# Revit family: C-Channel
name_source: partatom
category: Structural Framing
revit_build: Autodesk Revit Architecture 2012 (Build: 20110210_1515)
units: mm (PartAtom-declared; Revit-internal decimal feet)

## types (32) — shared parameters
Assembly Code = B10

## per-type parameters (varying)
| type | A | W | bf | d | tf | tw | x |
| C15X50 | 14.7 in² | 50 | 0' - 3 3/4" | 1' - 3" | 0' - 0 5/8" | 0' - 0 11/16" | 0' - 0 13/16" |
| C15X40 | 11.8 in² | 40 | 0' - 3 1/2" | 1' - 3" | 0' - 0 5/8" | 0' - 0 1/2" | 0' - 0 3/4" |
| C15X33.9 | 10 in² | 33.9 | 0' - 3 3/8" | 1' - 3" | 0' - 0 5/8" | 0' - 0 3/8" | 0' - 0 13/16" |
| C12X30 | 8.81 in² | 30 | 0' - 3 3/16" | 1' - 0" | 0' - 0 1/2" | 0' - 0 1/2" | 0' - 0 11/16" |
| C12X25 | 7.34 in² | 25 | 0' - 3 1/16" | 1' - 0" | 0' - 0 1/2" | 0' - 0 3/8" | 0' - 0 11/16" |
| C12X20.7 | 6.08 in² | 20.7 | 0' - 2 15/16" | 1' - 0" | 0' - 0 1/2" | 0' - 0 5/16" | 0' - 0 11/16" |
| C10X30 | 8.81 in² | 30 | 0' - 3" | 0' - 10" | 0' - 0 7/16" | 0' - 0 11/16" | 0' - 0 5/8" |
| C10X25 | 7.34 in² | 25 | 0' - 2 7/8" | 0' - 10" | 0' - 0 7/16" | 0' - 0 1/2" | 0' - 0 5/8" |
| C10X20 | 5.87 in² | 20 | 0' - 2 3/4" | 0' - 10" | 0' - 0 7/16" | 0' - 0 3/8" | 0' - 0 5/8" |
| C10X15.3 | 4.48 in² | 15.3 | 0' - 2 5/8" | 0' - 10" | 0' - 0 7/16" | 0' - 0 1/4" | 0' - 0 5/8" |
| C9X20 | 5.87 in² | 20 | 0' - 2 5/8" | 0' - 9" | 0' - 0 7/16" | 0' - 0 7/16" | 0' - 0 9/16" |
| C9X15 | 4.41 in² | 15 | 0' - 2 1/2" | 0' - 9" | 0' - 0 7/16" | 0' - 0 5/16" | 0' - 0 9/16" |
| C9X13.4 | 3.94 in² | 13.4 | 0' - 2 7/16" | 0' - 9" | 0' - 0 7/16" | 0' - 0 1/4" | 0' - 0 5/8" |
| C8X18.7 | 5.51 in² | 18.7 | 0' - 2 1/2" | 0' - 8" | 0' - 0 3/8" | 0' - 0 1/2" | 0' - 0 9/16" |
| C8X18.5 - Obsolete | 5.5 in² | 18.75 | 0' - 2 1/2" | 0' - 8" | 0' - 0 3/8" | 0' - 0 1/2" | 0' - 0 9/16" |
| C8X13.7 | 4.04 in² | 13.7 | 0' - 2 5/16" | 0' - 8" | 0' - 0 3/8" | 0' - 0 5/16" | 0' - 0 9/16" |
| C8X11.5 | 3.37 in² | 11.5 | 0' - 2 1/4" | 0' - 8" | 0' - 0 3/8" | 0' - 0 1/4" | 0' - 0 9/16" |
| C7X14.7 | 4.33 in² | 14.7 | 0' - 2 5/16" | 0' - 7" | 0' - 0 3/8" | 0' - 0 7/16" | 0' - 0 9/16" |
| C7X12.2 | 3.6 in² | 12.2 | 0' - 2 3/16" | 0' - 7" | 0' - 0 3/8" | 0' - 0 5/16" | 0' - 0 1/2" |
| C7X9.8 | 2.87 in² | 9.8 | 0' - 2 1/16" | 0' - 7" | 0' - 0 3/8" | 0' - 0 3/16" | 0' - 0 9/16" |
| C6X13 | 3.81 in² | 13 | 0' - 2 3/16" | 0' - 6" | 0' - 0 5/16" | 0' - 0 7/16" | 0' - 0 1/2" |
| C6X10.5 | 3.08 in² | 10.5 | 0' - 2" | 0' - 6" | 0' - 0 5/16" | 0' - 0 5/16" | 0' - 0 1/2" |
| C6X8.2 | 2.39 in² | 8.2 | 0' - 1 15/16" | 0' - 6" | 0' - 0 5/16" | 0' - 0 3/16" | 0' - 0 1/2" |
| C5X9 | 2.64 in² | 9 | 0' - 1 7/8" | 0' - 5" | 0' - 0 5/16" | 0' - 0 5/16" | 0' - 0 1/2" |
| C5X6.7 | 1.97 in² | 6.7 | 0' - 1 3/4" | 0' - 5" | 0' - 0 5/16" | 0' - 0 3/16" | 0' - 0 1/2" |
| C4X7.2 | 2.13 in² | 7.2 | 0' - 1 3/4" | 0' - 4" | 0' - 0 5/16" | 0' - 0 5/16" | 0' - 0 7/16" |
| C4X5.4 | 1.58 in² | 5.4 | 0' - 1 9/16" | 0' - 4" | 0' - 0 5/16" | 0' - 0 3/16" | 0' - 0 7/16" |
| C4X4.5 | 1.38 in² | 4.5 | 0' - 1 9/16" | 0' - 4" | 0' - 0 5/16" | 0' - 0 1/8" | 0' - 0 1/2" |
| C3X6 | 1.76 in² | 6 | 0' - 1 5/8" | 0' - 3" | 0' - 0 1/4" | 0' - 0 3/8" | 0' - 0 7/16" |
| C3X5 | 1.47 in² | 5 | 0' - 1 1/2" | 0' - 3" | 0' - 0 1/4" | 0' - 0 1/4" | 0' - 0 7/16" |
| C3X4.1 | 1.2 in² | 4.1 | 0' - 1 7/16" | 0' - 3" | 0' - 0 1/4" | 0' - 0 3/16" | 0' - 0 7/16" |
| C3X3.5 | 1.09 in² | 3.5 | 0' - 1 3/8" | 0' - 3" | 0' - 0 1/4" | 0' - 0 1/8" | 0' - 0 7/16" |

## geometry (parser evidence)
native form markers: Sweep x1
no freeform markers — native parametric forms only
